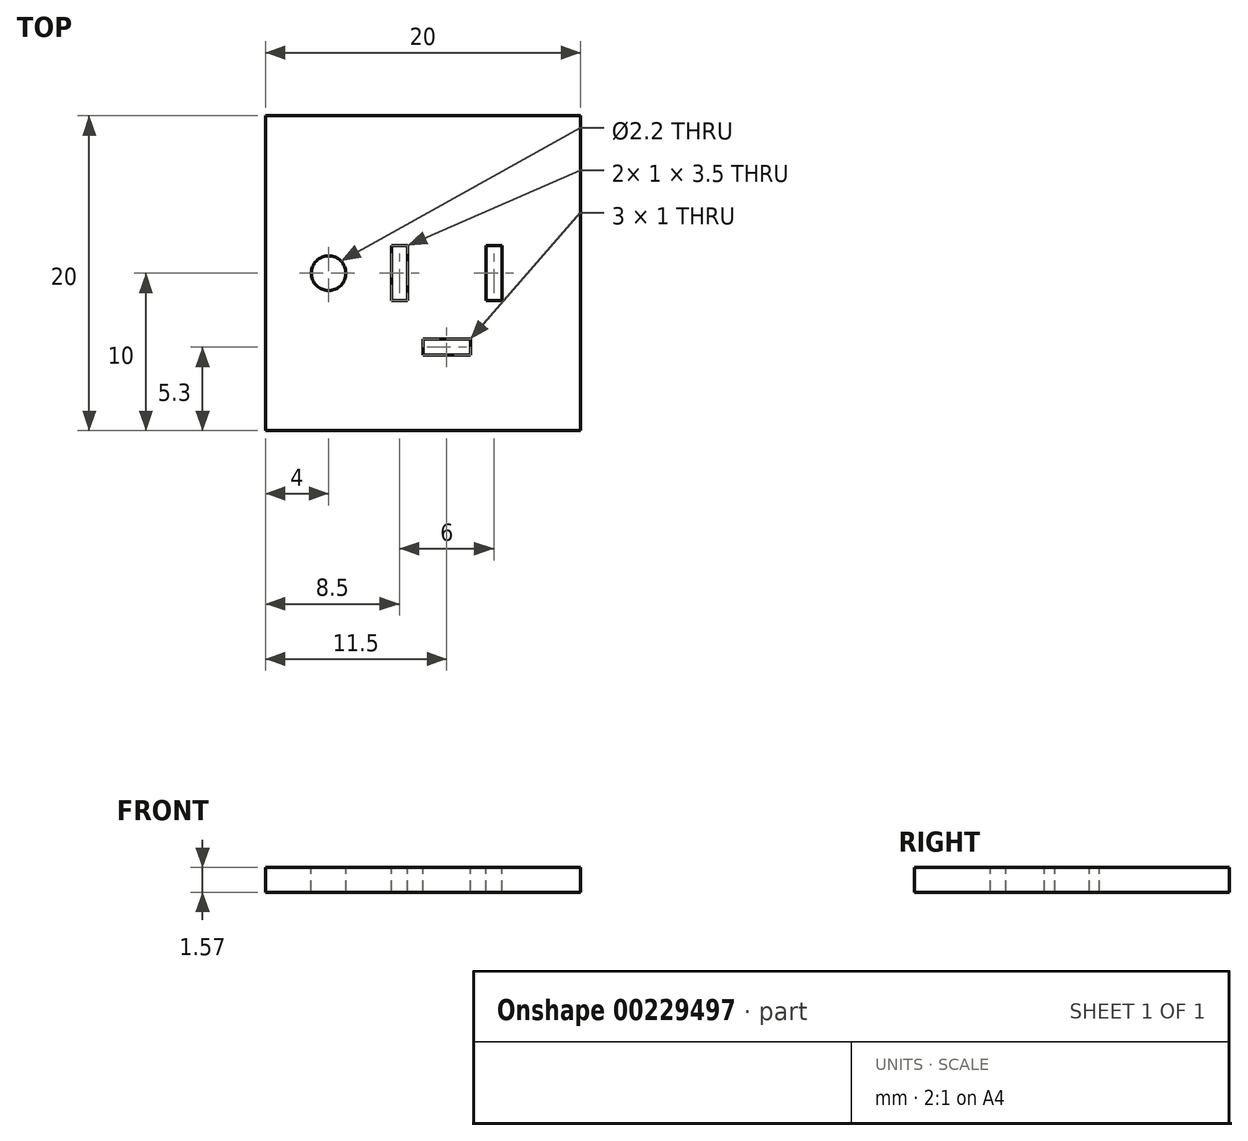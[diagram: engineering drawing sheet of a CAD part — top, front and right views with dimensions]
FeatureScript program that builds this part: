
annotation { "Feature Type Name" : "Feature", "Feature Type Description" : "" }
export const myFeature = defineFeature(function(context is Context, id is Id, definition is map)
    precondition{}
    {
        {
            var Q0;
            Q0=qCreatedBy(makeId("Top.planeOp"),FACE);
            var sketch = newSketch(context, id + "F0", { "sketchPlane" : qUnion([Q0])});
            skLineSegment(sketch, "E0.bottom", {"start": v(0, 10) * mm, "end": v(20, 10) * mm});
            skLineSegment(sketch, "E0.top", {"start": v(0, -10) * mm, "end": v(20, -10) * mm});
            skLineSegment(sketch, "E0.left", {"start": v(0, 10) * mm, "end": v(0, -10) * mm});
            skLineSegment(sketch, "E0.right", {"start": v(20, 10) * mm, "end": v(20, -10) * mm});
            skSolve(sketch);
        }
        {
            var Q0;
            Q0 = qSketchRegion(id + "F0", true);
            extrude(context, id + "F1", {"entities" : qUnion([Q0]), "depth" : 1.57 * mm});
        }
        {
            var Q0;
            Q0=makeQuery(id+"F1.opExtrude","CAP_FACE",FACE,{"disambiguationData":[OSD([sQuery(id+"F0.wireOp",EDGE,"E0.bottom"),sQuery(id+"F0.wireOp",EDGE,"E0.top"),sQuery(id+"F0.wireOp",EDGE,"E0.left"),sQuery(id+"F0.wireOp",EDGE,"E0.right")])],"isStart":false});
            var sketch = newSketch(context, id + "F2", { "sketchPlane" : qUnion([Q0])});
            skCircle(sketch, "E1", {"center": v(4, 0) * mm, "radius": 1.1 * mm});
            skLineSegment(sketch, "E2", {"start": v(0, 0) * mm, "end": v(20, 0) * mm, "construction": true});
            skLineSegment(sketch, "E3.bottom", {"start": v(9, 1.75) * mm, "end": v(8, 1.75) * mm});
            skLineSegment(sketch, "E3.top", {"start": v(9, -1.75) * mm, "end": v(8, -1.75) * mm});
            skLineSegment(sketch, "E3.left", {"start": v(9, 1.75) * mm, "end": v(9, -1.75) * mm});
            skLineSegment(sketch, "E3.right", {"start": v(8, 1.75) * mm, "end": v(8, -1.75) * mm});
            skPoint(sketch, "E3.middle", {"position": v(8.5, 0) * mm});
            skLineSegment(sketch, "E4.bottom", {"start": v(15, 1.75) * mm, "end": v(14, 1.75) * mm});
            skLineSegment(sketch, "E4.top", {"start": v(15, -1.75) * mm, "end": v(14, -1.75) * mm});
            skLineSegment(sketch, "E4.left", {"start": v(15, 1.75) * mm, "end": v(15, -1.75) * mm});
            skLineSegment(sketch, "E4.right", {"start": v(14, 1.75) * mm, "end": v(14, -1.75) * mm});
            skPoint(sketch, "E4.middle", {"position": v(14.5, 0) * mm});
            skLineSegment(sketch, "E5.bottom", {"start": v(13, -4.2) * mm, "end": v(10, -4.2) * mm});
            skLineSegment(sketch, "E5.top", {"start": v(13, -5.2) * mm, "end": v(10, -5.2) * mm});
            skLineSegment(sketch, "E5.left", {"start": v(13, -4.2) * mm, "end": v(13, -5.2) * mm});
            skLineSegment(sketch, "E5.right", {"start": v(10, -4.2) * mm, "end": v(10, -5.2) * mm});
            skPoint(sketch, "E5.middle", {"position": v(11.5, -4.7) * mm});
            skSolve(sketch);
        }
        {
            var Q0;
            Q0 = qSketchRegion(id + "F2", true);
            extrude(context, id + "F3", {"entities" : qUnion([Q0]), "operationType" : NewBodyOperationType.REMOVE, "oppositeDirection" : true, "depth" : 25 * mm});
        }
    });
